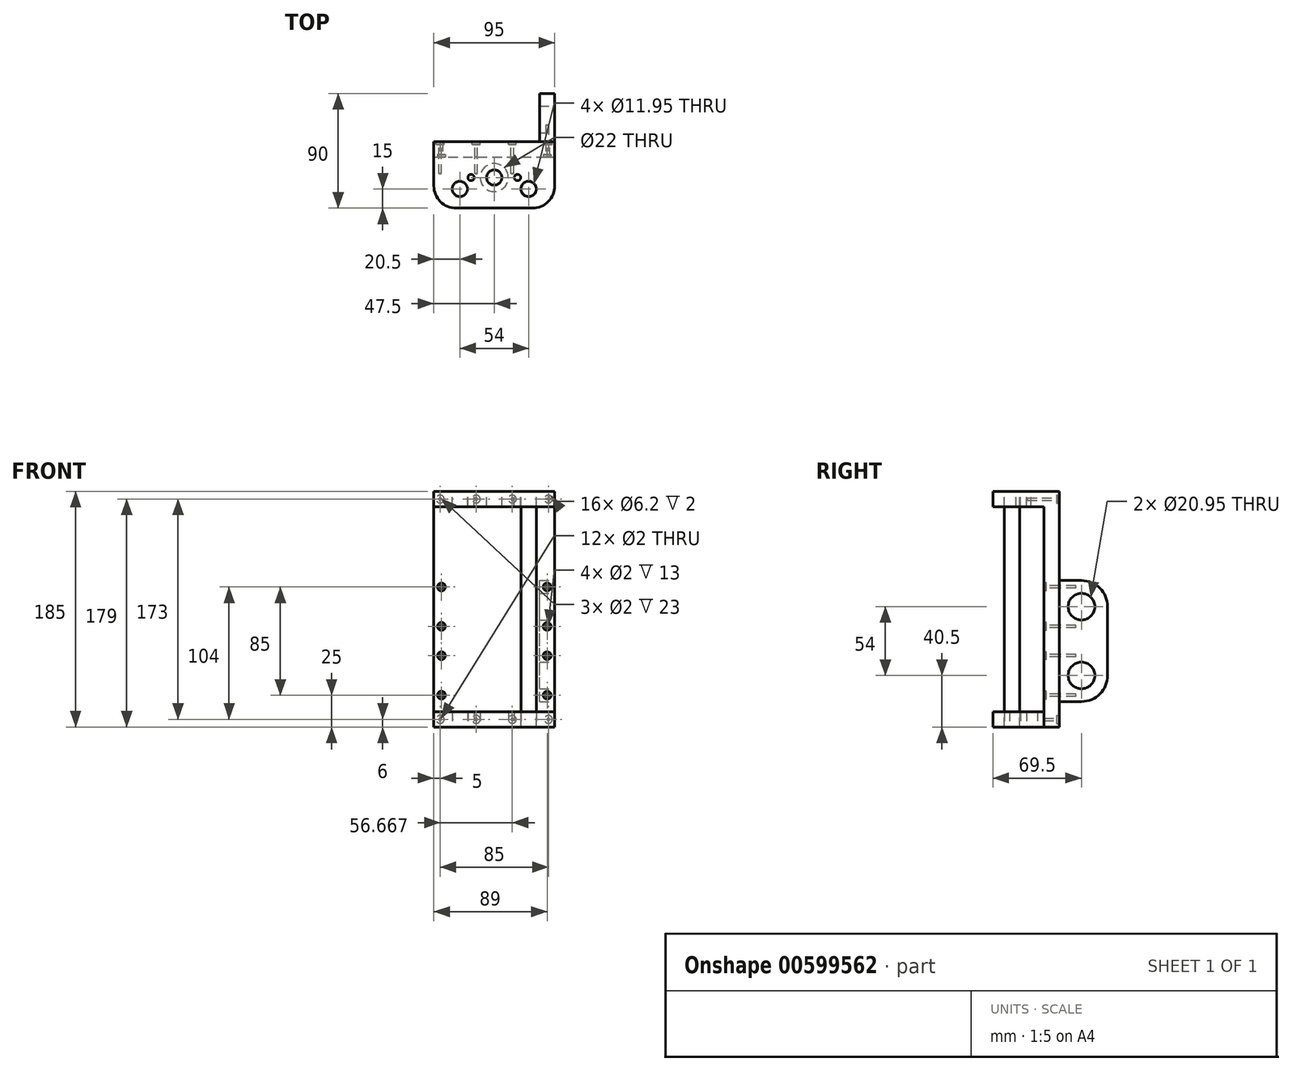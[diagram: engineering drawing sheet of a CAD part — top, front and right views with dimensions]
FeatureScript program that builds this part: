
annotation { "Feature Type Name" : "Feature", "Feature Type Description" : "" }
export const myFeature = defineFeature(function(context is Context, id is Id, definition is map)
    precondition{}
    {
        {
            var Q0;
            Q0=qCreatedBy(makeId("Front.planeOp"),FACE);
            var sketch = newSketch(context, id + "F0", { "sketchPlane" : qUnion([Q0])});
            skLineSegment(sketch, "E0.bottom", {"start": v(-47.5, 0) * mm, "end": v(47.5, 0) * mm});
            skLineSegment(sketch, "E0.top", {"start": v(-47.5, 185) * mm, "end": v(47.5, 185) * mm});
            skLineSegment(sketch, "E0.left", {"start": v(-47.5, 0) * mm, "end": v(-47.5, 185) * mm});
            skLineSegment(sketch, "E0.right", {"start": v(47.5, 0) * mm, "end": v(47.5, 185) * mm});
            skSolve(sketch);
        }
        {
            var Q0;
            Q0 = qSketchRegion(id + "F0", true);
            extrude(context, id + "F1", {"entities" : qUnion([Q0]), "oppositeDirection" : true, "depth" : 12 * mm, "offsetDistance" : 25 * mm});
        }
        {
            var Q0;
            Q0=makeQuery(id+"F1.opExtrude","SWEPT_FACE",FACE,{"disambiguationData":[OSD([sQuery(id+"F0.wireOp",EDGE,"E0.top")])]});
            var sketch = newSketch(context, id + "F2", { "sketchPlane" : qUnion([Q0])});
            skLineSegment(sketch, "E1.bottom", {"start": v(-47.5, 0) * mm, "end": v(47.5, 0) * mm});
            skLineSegment(sketch, "E1.top", {"start": v(-30, -40) * mm, "end": v(30, -40) * mm});
            skLineSegment(sketch, "E1.left", {"start": v(-47.5, 0) * mm, "end": v(-47.5, -22.5) * mm});
            skLineSegment(sketch, "E1.right", {"start": v(47.5, 0) * mm, "end": v(47.5, -22.5) * mm});
            skLineSegment(sketch, "E2", {"start": v(0, 0) * mm, "end": v(0, -40) * mm, "construction": true});
            skCircle(sketch, "E3", {"center": v(-27, -25) * mm, "radius": 5.97 * mm});
            skCircle(sketch, "E4.MirrorC", {"center": v(27, -25) * mm, "radius": 5.97 * mm});
            skPoint(sketch, "E5.visualSharp", {"position": v(-47.5, -40) * mm});
            skArc(sketch, "E5.filletArc", {"start": v(-47.5, -22.5) * mm, "mid": v(-42.37, -34.87) * mm, "end": v(-30, -40) * mm});
            skPoint(sketch, "E6.visualSharp", {"position": v(47.5, -40) * mm});
            skArc(sketch, "E6.filletArc", {"start": v(30, -40) * mm, "mid": v(42.37, -34.87) * mm, "end": v(47.5, -22.5) * mm});
            skCircle(sketch, "E7", {"center": v(0, -16) * mm, "radius": 6 * mm});
            skCircle(sketch, "E8", {"center": v(-18.25, -16) * mm, "radius": 2.5 * mm});
            skCircle(sketch, "E9.MirrorC", {"center": v(18.25, -16) * mm, "radius": 2.5 * mm});
            skSolve(sketch);
        }
        {
            var Q0;
            Q0 = qSketchRegion(id + "F2", true);
            extrude(context, id + "F3", {"entities" : qUnion([Q0]), "oppositeDirection" : true, "depth" : 12 * mm, "offsetDistance" : 25 * mm});
        }
        {
            var Q0;
            Q0=makeQuery(id+"F1.opExtrude","CAP_FACE",FACE,{"disambiguationData":[OSD([sQuery(id+"F0.wireOp",EDGE,"E0.bottom"),sQuery(id+"F0.wireOp",EDGE,"E0.top"),sQuery(id+"F0.wireOp",EDGE,"E0.left"),sQuery(id+"F0.wireOp",EDGE,"E0.right")])],"isStart":false});
            var sketch = newSketch(context, id + "F4", { "sketchPlane" : qUnion([Q0])});
            skCircle(sketch, "E10", {"center": v(-42.5, 179) * mm, "radius": 3.1 * mm});
            skCircle(sketch, "E11", {"center": v(-14.17, 179) * mm, "radius": 3.1 * mm});
            skLineSegment(sketch, "E12", {"start": v(-42.5, 179) * mm, "end": v(-14.17, 179) * mm, "construction": true});
            skLineSegment(sketch, "E13", {"start": v(0, 185) * mm, "end": v(0, 0) * mm, "construction": true});
            skLineSegment(sketch, "E14", {"start": v(47.5, 92.5) * mm, "end": v(-47.5, 92.5) * mm, "construction": true});
            skCircle(sketch, "E15.MirrorC", {"center": v(14.17, 179) * mm, "radius": 3.1 * mm});
            skCircle(sketch, "E16.MirrorC", {"center": v(42.5, 179) * mm, "radius": 3.1 * mm});
            skCircle(sketch, "E17.MirrorC", {"center": v(-42.5, 6) * mm, "radius": 3.1 * mm});
            skCircle(sketch, "E18.MirrorC", {"center": v(-14.17, 6) * mm, "radius": 3.1 * mm});
            skCircle(sketch, "E19.MirrorC", {"center": v(14.17, 6) * mm, "radius": 3.1 * mm});
            skCircle(sketch, "E20.MirrorC", {"center": v(42.5, 6) * mm, "radius": 3.1 * mm});
            skLineSegment(sketch, "E21", {"start": v(-14.17, 179) * mm, "end": v(14.17, 179) * mm, "construction": true});
            skSolve(sketch);
        }
        {
            var Q0;
            Q0 = qSketchRegion(id + "F4", true);
            extrude(context, id + "F5", {"entities" : qUnion([Q0]), "operationType" : NewBodyOperationType.REMOVE, "oppositeDirection" : true, "depth" : 2 * mm, "offsetDistance" : 25 * mm});
        }
        {
            var Q0;
            Q0=makeQuery(id+"F1.opExtrude","CAP_FACE",FACE,{"disambiguationData":[OSD([sQuery(id+"F0.wireOp",EDGE,"E0.bottom"),sQuery(id+"F0.wireOp",EDGE,"E0.top"),sQuery(id+"F0.wireOp",EDGE,"E0.left"),sQuery(id+"F0.wireOp",EDGE,"E0.right")])],"isStart":false});
            var sketch = newSketch(context, id + "F6", { "sketchPlane" : qUnion([Q0])});
            skCircle(sketch, "E22", {"center": v(-42.5, 179) * mm, "radius": 1 * mm});
            skCircle(sketch, "E23", {"center": v(-14.17, 179) * mm, "radius": 1 * mm});
            skCircle(sketch, "E24", {"center": v(14.17, 179) * mm, "radius": 1 * mm});
            skCircle(sketch, "E25", {"center": v(42.5, 179) * mm, "radius": 1 * mm});
            skCircle(sketch, "E26", {"center": v(-42.5, 6) * mm, "radius": 1 * mm});
            skCircle(sketch, "E27", {"center": v(-14.17, 6) * mm, "radius": 1 * mm});
            skCircle(sketch, "E28", {"center": v(14.17, 6) * mm, "radius": 1 * mm});
            skCircle(sketch, "E29", {"center": v(42.5, 6) * mm, "radius": 1 * mm});
            skSolve(sketch);
        }
        {
            var Q0;
            Q0 = qSketchRegion(id + "F6", true);
            extrude(context, id + "F7", {"entities" : qUnion([Q0]), "operationType" : NewBodyOperationType.REMOVE, "oppositeDirection" : true, "depth" : 25 * mm, "offsetDistance" : 25 * mm});
        }
        {
            var Q0;
            Q0=makeQuery(id+"F3.opExtrude","CAP_FACE",FACE,{"disambiguationData":[OSD([sQuery(id+"F2.wireOp",EDGE,"E1.bottom"),sQuery(id+"F2.wireOp",EDGE,"E1.top"),sQuery(id+"F2.wireOp",EDGE,"E1.left"),sQuery(id+"F2.wireOp",EDGE,"E1.right"),sQuery(id+"F2.wireOp",EDGE,"E3"),sQuery(id+"F2.wireOp",EDGE,"E4.MirrorC"),sQuery(id+"F2.wireOp",EDGE,"E5.filletArc"),sQuery(id+"F2.wireOp",EDGE,"E6.filletArc")])],"isStart":true});
            var sketch = newSketch(context, id + "F8", { "sketchPlane" : qUnion([Q0])});
            skCircle(sketch, "E30", {"center": v(27, -25) * mm, "radius": 6 * mm});
            skSolve(sketch);
        }
        {
            var Q0;
            Q0 = qSketchRegion(id + "F8", true);
            extrude(context, id + "F9", {"entities" : qUnion([Q0]), "oppositeDirection" : true, "depth" : 185 * mm, "offsetDistance" : 25 * mm});
        }
        {
            var Q0;
            Q0=makeQuery(id+"F1.opExtrude","CAP_FACE",FACE,{"disambiguationData":[OSD([sQuery(id+"F0.wireOp",EDGE,"E0.bottom"),sQuery(id+"F0.wireOp",EDGE,"E0.top"),sQuery(id+"F0.wireOp",EDGE,"E0.left"),sQuery(id+"F0.wireOp",EDGE,"E0.right")])],"isStart":false});
            var sketch = newSketch(context, id + "F10", { "sketchPlane" : qUnion([Q0])});
            skCircle(sketch, "E31", {"center": v(-42.5, 179) * mm, "radius": 3 * mm});
            skSolve(sketch);
        }
        {
            var Q0;
            Q0 = qSketchRegion(id + "F10", true);
            extrude(context, id + "F11", {"entities" : qUnion([Q0]), "oppositeDirection" : true, "depth" : 2 * mm, "offsetDistance" : 25 * mm});
        }
        {
            var Q0;
            Q0=makeQuery(id+"F11.opExtrude","CAP_FACE",FACE,{"disambiguationData":[OSD([sQuery(id+"F10.wireOp",EDGE,"E31")])],"isStart":false});
            var sketch = newSketch(context, id + "F12", { "sketchPlane" : qUnion([Q0])});
            skCircle(sketch, "E32", {"center": v(42.5, 179) * mm, "radius": 1 * mm});
            skSolve(sketch);
        }
        {
            var Q0;
            Q0 = qSketchRegion(id + "F12", true);
            extrude(context, id + "F13", {"entities" : qUnion([Q0]), "operationType" : NewBodyOperationType.ADD, "depth" : 23 * mm, "offsetDistance" : 25 * mm});
        }
        {
            var Q0;
            Q0=makeQuery(id+"F11.opExtrude","CAP_FACE",FACE,{"disambiguationData":[OSD([sQuery(id+"F10.wireOp",EDGE,"E31")])],"isStart":true});
            var sketch = newSketch(context, id + "F14", { "sketchPlane" : qUnion([Q0])});
            skLineSegment(sketch, "E33.bottom", {"start": v(-42.85, 181.35) * mm, "end": v(-42.15, 181.35) * mm});
            skLineSegment(sketch, "E33.top", {"start": v(-42.85, 176.65) * mm, "end": v(-42.15, 176.65) * mm});
            skLineSegment(sketch, "E33.left", {"start": v(-42.85, 181.35) * mm, "end": v(-42.85, 179.35) * mm});
            skLineSegment(sketch, "E33.right", {"start": v(-42.15, 181.35) * mm, "end": v(-42.15, 179.35) * mm});
            skLineSegment(sketch, "E34.bottom", {"start": v(-44.85, 179.35) * mm, "end": v(-42.85, 179.35) * mm});
            skLineSegment(sketch, "E34.top", {"start": v(-44.85, 178.65) * mm, "end": v(-42.85, 178.65) * mm});
            skLineSegment(sketch, "E34.left", {"start": v(-44.85, 179.35) * mm, "end": v(-44.85, 178.65) * mm});
            skLineSegment(sketch, "E34.right", {"start": v(-40.15, 179.35) * mm, "end": v(-40.15, 178.65) * mm});
            skLineSegment(sketch, "E35", {"start": v(-42.5, 179) * mm, "end": v(-40.15, 179) * mm, "construction": true});
            skLineSegment(sketch, "E36", {"start": v(-42.5, 181.35) * mm, "end": v(-42.5, 179) * mm, "construction": true});
            skLineSegment(sketch, "E37.trimOffspring", {"start": v(-42.15, 179.35) * mm, "end": v(-40.15, 179.35) * mm});
            skLineSegment(sketch, "E38.trimOffspring", {"start": v(-42.85, 178.65) * mm, "end": v(-42.85, 176.65) * mm});
            skLineSegment(sketch, "E39.trimOffspring", {"start": v(-42.15, 178.65) * mm, "end": v(-40.15, 178.65) * mm});
            skLineSegment(sketch, "E40.trimOffspring", {"start": v(-42.15, 178.65) * mm, "end": v(-42.15, 176.65) * mm});
            skSolve(sketch);
        }
        {
            var Q0;
            Q0 = qSketchRegion(id + "F14", true);
            extrude(context, id + "F15", {"entities" : qUnion([Q0]), "operationType" : NewBodyOperationType.REMOVE, "oppositeDirection" : true, "depth" : 1.5 * mm, "offsetDistance" : 25 * mm});
        }
        {
            var Q0;
            Q0=makeQuery(id+"F1.opExtrude","SWEPT_FACE",FACE,{"disambiguationData":[OSD([sQuery(id+"F0.wireOp",EDGE,"E0.right")])]});
            var sketch = newSketch(context, id + "F16", { "sketchPlane" : qUnion([Q0])});
            skLineSegment(sketch, "E41.bottom", {"start": v(12, 20) * mm, "end": v(29.5, 20) * mm});
            skLineSegment(sketch, "E41.top", {"start": v(12, 115) * mm, "end": v(29.5, 115) * mm});
            skLineSegment(sketch, "E41.left", {"start": v(12, 20) * mm, "end": v(12, 115) * mm});
            skLineSegment(sketch, "E41.right", {"start": v(50, 40.5) * mm, "end": v(50, 94.5) * mm});
            skPoint(sketch, "E42.visualSharp", {"position": v(50, 115) * mm});
            skArc(sketch, "E42.filletArc", {"start": v(50, 94.5) * mm, "mid": v(44, 109) * mm, "end": v(29.5, 115) * mm});
            skPoint(sketch, "E43.visualSharp", {"position": v(50, 20) * mm});
            skArc(sketch, "E43.filletArc", {"start": v(29.5, 20) * mm, "mid": v(44, 26) * mm, "end": v(50, 40.5) * mm});
            skCircle(sketch, "E44", {"center": v(29.5, 40.5) * mm, "radius": 10.47 * mm});
            skLineSegment(sketch, "E45", {"start": v(12, 67.5) * mm, "end": v(50, 67.5) * mm, "construction": true});
            skCircle(sketch, "E46.MirrorC", {"center": v(29.5, 94.5) * mm, "radius": 10.47 * mm});
            skSolve(sketch);
        }
        {
            var Q0;
            Q0 = qSketchRegion(id + "F16", true);
            extrude(context, id + "F17", {"entities" : qUnion([Q0]), "oppositeDirection" : true, "depth" : 12 * mm, "offsetDistance" : 25 * mm});
        }
        {
            var Q0;
            Q0=makeQuery(id+"F1.opExtrude","CAP_FACE",FACE,{"disambiguationData":[OSD([sQuery(id+"F0.wireOp",EDGE,"E0.bottom"),sQuery(id+"F0.wireOp",EDGE,"E0.top"),sQuery(id+"F0.wireOp",EDGE,"E0.left"),sQuery(id+"F0.wireOp",EDGE,"E0.right")])],"isStart":true});
            var sketch = newSketch(context, id + "F18", { "sketchPlane" : qUnion([Q0])});
            skCircle(sketch, "E47", {"center": v(41.5, 25) * mm, "radius": 3.1 * mm});
            skCircle(sketch, "E48", {"center": v(41.5, 56) * mm, "radius": 3.1 * mm});
            skCircle(sketch, "E49", {"center": v(41.5, 79) * mm, "radius": 3.1 * mm});
            skCircle(sketch, "E50", {"center": v(41.5, 110) * mm, "radius": 3.1 * mm});
            skLineSegment(sketch, "E51", {"start": v(41.5, 25) * mm, "end": v(41.5, 56) * mm, "construction": true});
            skLineSegment(sketch, "E52", {"start": v(41.5, 79) * mm, "end": v(41.5, 56) * mm, "construction": true});
            skLineSegment(sketch, "E53", {"start": v(41.5, 110) * mm, "end": v(41.5, 79) * mm, "construction": true});
            skLineSegment(sketch, "E54", {"start": v(0, 0) * mm, "end": v(0, 185) * mm, "construction": true});
            skCircle(sketch, "E55.MirrorC", {"center": v(-41.5, 25) * mm, "radius": 3.1 * mm});
            skCircle(sketch, "E56.MirrorC", {"center": v(-41.5, 56) * mm, "radius": 3.1 * mm});
            skCircle(sketch, "E57.MirrorC", {"center": v(-41.5, 79) * mm, "radius": 3.1 * mm});
            skCircle(sketch, "E58.MirrorC", {"center": v(-41.5, 110) * mm, "radius": 3.1 * mm});
            skSolve(sketch);
        }
        {
            var Q0;
            Q0 = qSketchRegion(id + "F18", true);
            extrude(context, id + "F19", {"entities" : qUnion([Q0]), "operationType" : NewBodyOperationType.REMOVE, "oppositeDirection" : true, "depth" : 2 * mm, "offsetDistance" : 25 * mm});
        }
        {
            var Q0;
            Q0=makeQuery(id+"F1.opExtrude","CAP_FACE",FACE,{"disambiguationData":[OSD([sQuery(id+"F0.wireOp",EDGE,"E0.bottom"),sQuery(id+"F0.wireOp",EDGE,"E0.top"),sQuery(id+"F0.wireOp",EDGE,"E0.left"),sQuery(id+"F0.wireOp",EDGE,"E0.right")])],"isStart":true});
            var sketch = newSketch(context, id + "F20", { "sketchPlane" : qUnion([Q0])});
            skCircle(sketch, "E59", {"center": v(-41.5, 25) * mm, "radius": 1 * mm});
            skCircle(sketch, "E60", {"center": v(-41.5, 56) * mm, "radius": 1 * mm});
            skCircle(sketch, "E61", {"center": v(-41.5, 79) * mm, "radius": 1 * mm});
            skCircle(sketch, "E62", {"center": v(-41.5, 110) * mm, "radius": 1 * mm});
            skCircle(sketch, "E63", {"center": v(41.5, 110) * mm, "radius": 1 * mm});
            skCircle(sketch, "E64", {"center": v(41.5, 79) * mm, "radius": 1 * mm});
            skCircle(sketch, "E65", {"center": v(41.5, 56) * mm, "radius": 1 * mm});
            skCircle(sketch, "E66", {"center": v(41.5, 25) * mm, "radius": 1 * mm});
            skSolve(sketch);
        }
        {
            var Q0;
            Q0 = qSketchRegion(id + "F20", true);
            extrude(context, id + "F21", {"entities" : qUnion([Q0]), "operationType" : NewBodyOperationType.REMOVE, "oppositeDirection" : true, "depth" : 25 * mm, "offsetDistance" : 25 * mm});
        }
        {
            var Q0;
            Q0=makeQuery(id+"F1.opExtrude","SWEPT_FACE",FACE,{"disambiguationData":[OSD([sQuery(id+"F0.wireOp",EDGE,"E0.bottom")])]});
            var sketch = newSketch(context, id + "F22", { "sketchPlane" : qUnion([Q0])});
            skLineSegment(sketch, "E67.0", {"start": v(-47.5, 0) * mm, "end": v(47.5, 0) * mm});
            skArc(sketch, "E67.1", {"start": v(47.5, 22.5) * mm, "mid": v(42.37, 34.87) * mm, "end": v(30, 40) * mm});
            skLineSegment(sketch, "E67.2", {"start": v(30, 40) * mm, "end": v(-30, 40) * mm});
            skLineSegment(sketch, "E67.3", {"start": v(47.5, 0) * mm, "end": v(47.5, 22.5) * mm});
            skArc(sketch, "E67.4", {"start": v(-30, 40) * mm, "mid": v(-42.37, 34.87) * mm, "end": v(-47.5, 22.5) * mm});
            skLineSegment(sketch, "E67.5", {"start": v(-47.5, 22.5) * mm, "end": v(-47.5, 0) * mm});
            skCircle(sketch, "E68.0", {"center": v(-27, 25) * mm, "radius": 5.97 * mm});
            skCircle(sketch, "E69.0", {"center": v(27, 25) * mm, "radius": 5.97 * mm});
            skCircle(sketch, "E70.0", {"center": v(-18.25, 16) * mm, "radius": 2.5 * mm});
            skCircle(sketch, "E71.0", {"center": v(18.25, 16) * mm, "radius": 2.5 * mm});
            skCircle(sketch, "E72.0", {"center": v(0, 16) * mm, "radius": 11 * mm});
            skSolve(sketch);
        }
        {
            var Q0;
            Q0 = qSketchRegion(id + "F22", true);
            extrude(context, id + "F23", {"entities" : qUnion([Q0]), "oppositeDirection" : true, "depth" : 12 * mm, "offsetDistance" : 25 * mm});
        }
    });
